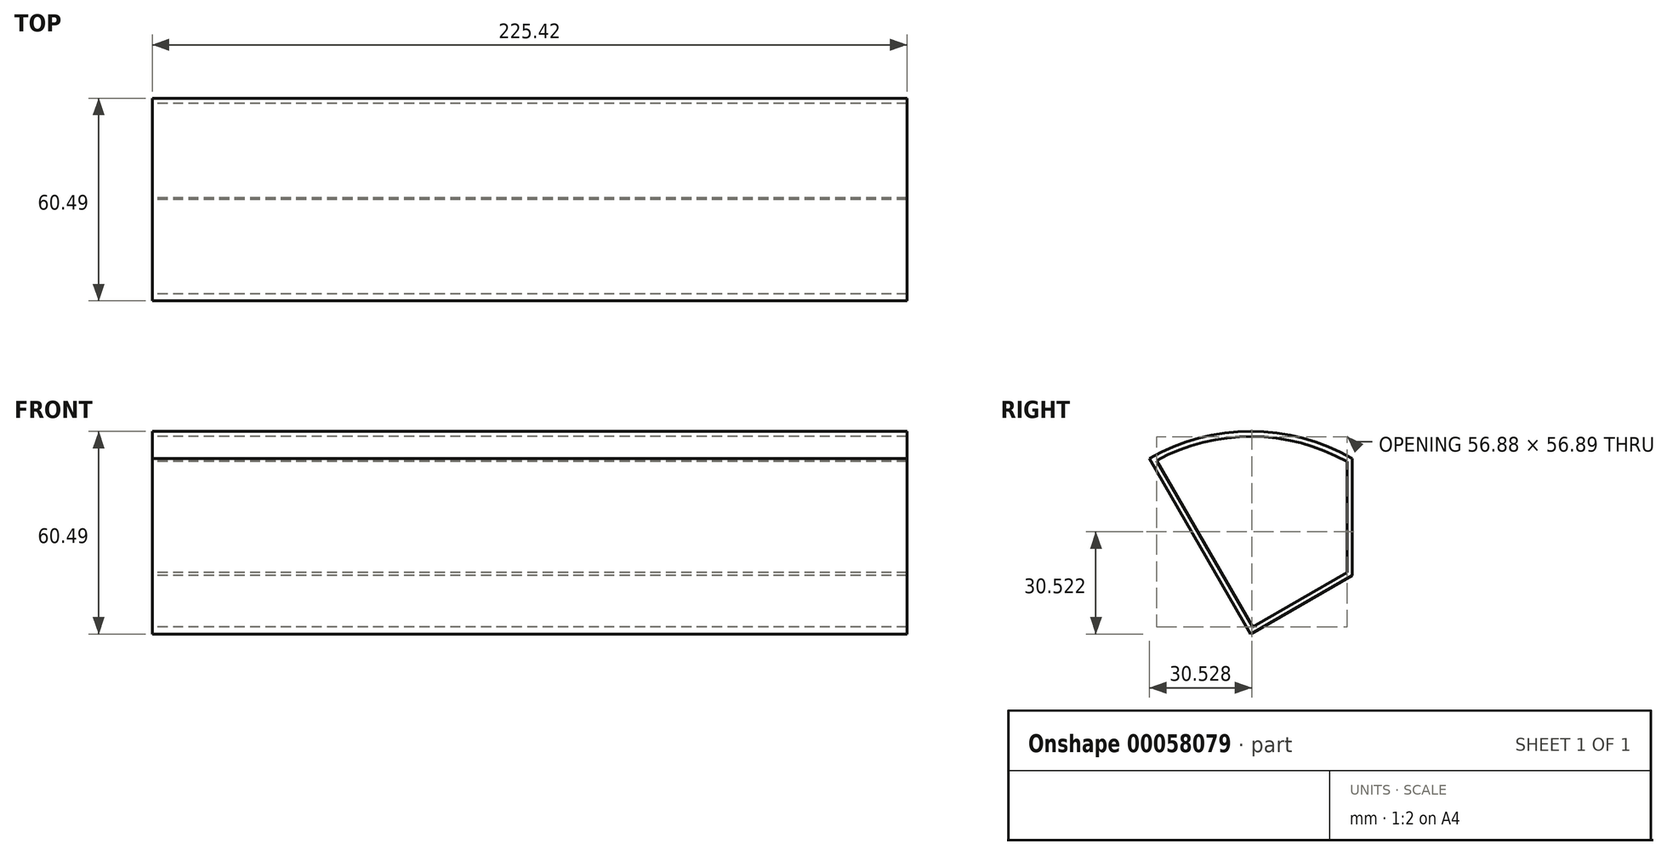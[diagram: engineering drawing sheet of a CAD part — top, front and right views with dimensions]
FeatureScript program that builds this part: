
annotation { "Feature Type Name" : "Feature", "Feature Type Description" : "" }
export const myFeature = defineFeature(function(context is Context, id is Id, definition is map)
    precondition{}
    {
        {
            var Q0;
            Q0=qCreatedBy(makeId("Right.planeOp"),FACE);
            var sketch = newSketch(context, id + "F0", { "sketchPlane" : qUnion([Q0])});
            skLineSegment(sketch, "E0", {"start": v(-30.25, -17.46) * mm, "end": v(0, 0) * mm});
            skLineSegment(sketch, "E1", {"start": v(0, 0) * mm, "end": v(0, 34.93) * mm});
            skArc(sketch, "E2", {"start": v(0, 34.92) * mm, "mid": v(-30.25, 43.03) * mm, "end": v(-60.5, 34.92) * mm});
            skLineSegment(sketch, "E3", {"start": v(0, 34.93) * mm, "end": v(-30.25, -17.46) * mm, "construction": true});
            skPoint(sketch, "E4", {"position": v(-15.12, 8.73) * mm});
            skLineSegment(sketch, "E5", {"start": v(0, 0) * mm, "end": v(-60.5, 34.93) * mm, "construction": true});
            skLineSegment(sketch, "E6", {"start": v(0, 34.93) * mm, "end": v(-60.5, 34.92) * mm, "construction": true});
            skLineSegment(sketch, "E7", {"start": v(-60.5, 34.92) * mm, "end": v(-30.25, -17.46) * mm});
            skSolve(sketch);
        }
        {
            var Q0;
            Q0=qSketchRegion(id+"F0",true);
            extrude(context, id + "F1", {"entities" : qUnion([Q0]), "endBound" : BoundingType.SYMMETRIC, "depth" : 225.42 * mm});
        }
        {
            var Q0;
            Q0=makeQuery(id+"F1.opExtrude","CAP_FACE",FACE,{"disambiguationData":[OSD([sQuery(id+"F0.wireOp",EDGE,"E0"),sQuery(id+"F0.wireOp",EDGE,"E1"),sQuery(id+"F0.wireOp",EDGE,"E2"),sQuery(id+"F0.wireOp",EDGE,"c3c49b80-8560-441d-a98b-bc6df337408e")])],"isStart":true});
            var Q1;
            Q1=makeQuery(id+"F1.opExtrude","CAP_FACE",FACE,{"disambiguationData":[OSD([sQuery(id+"F0.wireOp",EDGE,"E0"),sQuery(id+"F0.wireOp",EDGE,"E1"),sQuery(id+"F0.wireOp",EDGE,"E2"),sQuery(id+"F0.wireOp",EDGE,"c3c49b80-8560-441d-a98b-bc6df337408e")])],"isStart":false});
            shell(context, id + "F2", {"entities" : qUnion([Q0, Q1]), "thickness" : 1.52 * mm});
        }
    });
